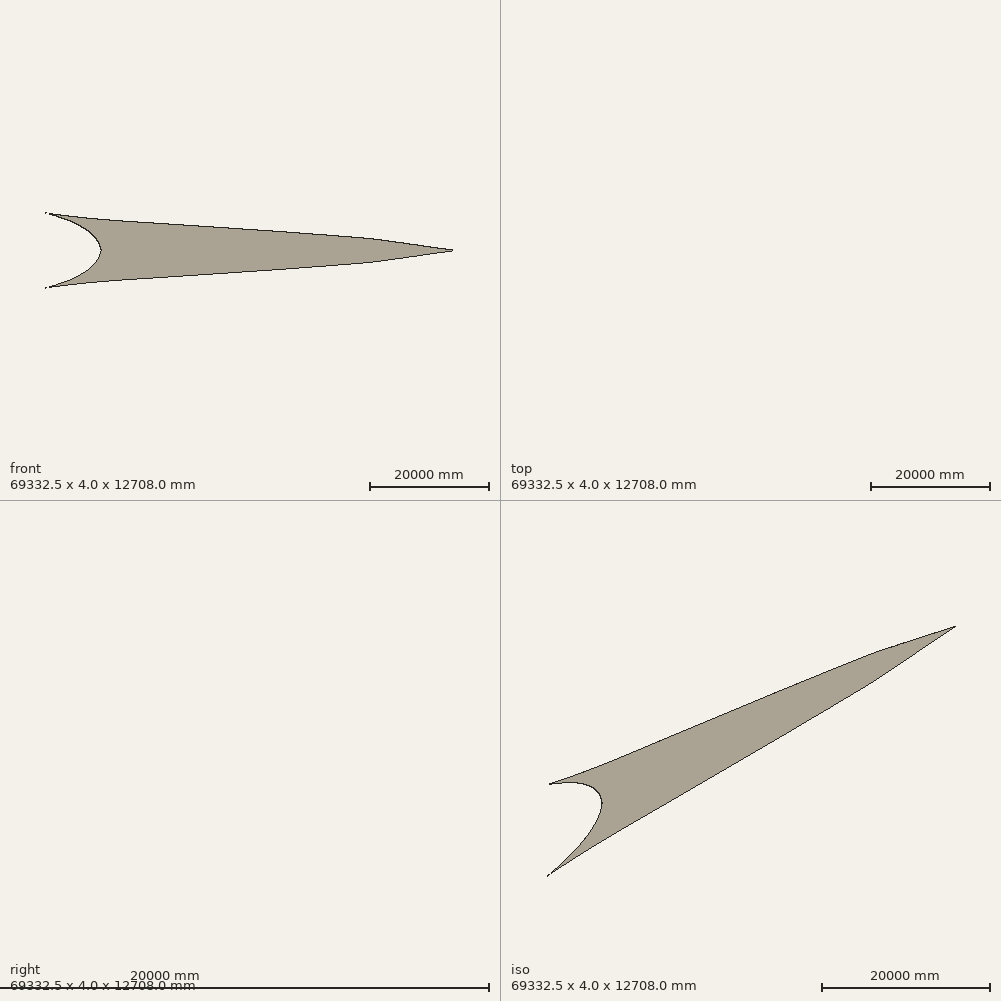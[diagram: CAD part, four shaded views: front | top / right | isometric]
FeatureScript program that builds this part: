
annotation { "Feature Type Name" : "Feature", "Feature Type Description" : "" }
export const myFeature = defineFeature(function(context is Context, id is Id, definition is map)
    precondition{}
    {
        {
            var Q0;
            Q0=qCreatedBy(makeId("Front.planeOp"),FACE);
            var sketch = newSketch(context, id + "F0", { "sketchPlane" : qUnion([Q0])});
            skLineSegment(sketch, "E0", {"start": v(34666.25, 0) * mm, "end": v(34435.52, -40.51) * mm});
            skLineSegment(sketch, "E1", {"start": v(34435.52, -40.51) * mm, "end": v(33954, -111.84) * mm});
            skLineSegment(sketch, "E2", {"start": v(33954, -111.84) * mm, "end": v(33694.2, -143.51) * mm});
            skLineSegment(sketch, "E3", {"start": v(33694.2, -143.51) * mm, "end": v(33434.53, -176) * mm});
            skLineSegment(sketch, "E4", {"start": v(33434.53, -176) * mm, "end": v(33084.57, -227.86) * mm});
            skLineSegment(sketch, "E5", {"start": v(33084.57, -227.86) * mm, "end": v(32734.78, -281.15) * mm});
            skLineSegment(sketch, "E6", {"start": v(32734.78, -281.15) * mm, "end": v(32207.2, -349.73) * mm});
            skLineSegment(sketch, "E7", {"start": v(32207.2, -349.73) * mm, "end": v(31403.65, -459.2) * mm});
            skLineSegment(sketch, "E8", {"start": v(31403.65, -459.2) * mm, "end": v(31005.5, -519.4) * mm});
            skLineSegment(sketch, "E9", {"start": v(31005.5, -519.4) * mm, "end": v(30607.23, -578.56) * mm});
            skLineSegment(sketch, "E10", {"start": v(30607.23, -578.56) * mm, "end": v(30171.5, -637.67) * mm});
            skLineSegment(sketch, "E11", {"start": v(30171.5, -637.67) * mm, "end": v(29735.68, -696.42) * mm});
            skLineSegment(sketch, "E12", {"start": v(29735.68, -696.42) * mm, "end": v(29204.16, -775.3) * mm});
            skLineSegment(sketch, "E13", {"start": v(29204.16, -775.3) * mm, "end": v(28673, -856.67) * mm});
            skLineSegment(sketch, "E14", {"start": v(28673, -856.67) * mm, "end": v(27858.21, -972.72) * mm});
            skLineSegment(sketch, "E15", {"start": v(27858.21, -972.72) * mm, "end": v(27293.5, -1049.15) * mm});
            skLineSegment(sketch, "E16", {"start": v(27293.5, -1049.15) * mm, "end": v(26729.36, -1129.59) * mm});
            skLineSegment(sketch, "E17", {"start": v(26729.36, -1129.59) * mm, "end": v(26203.07, -1212.27) * mm});
            skLineSegment(sketch, "E18", {"start": v(26203.07, -1212.27) * mm, "end": v(25676.63, -1293.72) * mm});
            skLineSegment(sketch, "E19", {"start": v(25676.63, -1293.72) * mm, "end": v(25053.6, -1378.03) * mm});
            skLineSegment(sketch, "E20", {"start": v(25053.6, -1378.03) * mm, "end": v(24429.9, -1457.76) * mm});
            skLineSegment(sketch, "E21", {"start": v(24429.9, -1457.76) * mm, "end": v(23395.89, -1601.9) * mm});
            skLineSegment(sketch, "E22", {"start": v(23395.89, -1601.9) * mm, "end": v(22319.9, -1757.22) * mm});
            skLineSegment(sketch, "E23", {"start": v(22319.9, -1757.22) * mm, "end": v(21652.28, -1849.27) * mm});
            skLineSegment(sketch, "E24", {"start": v(21652.28, -1849.27) * mm, "end": v(21071.92, -1921.36) * mm});
            skLineSegment(sketch, "E25", {"start": v(21071.92, -1921.36) * mm, "end": v(21056.24, -1795.32) * mm});
            skLineSegment(sketch, "E26", {"start": v(21056.24, -1795.32) * mm, "end": v(21071.92, -1921.36) * mm});
            skLineSegment(sketch, "E27", {"start": v(21071.92, -1921.36) * mm, "end": v(20056.25, -2031.26) * mm});
            skLineSegment(sketch, "E28", {"start": v(20056.25, -2031.26) * mm, "end": v(19038.87, -2123.26) * mm});
            skLineSegment(sketch, "E29", {"start": v(19038.87, -2123.26) * mm, "end": v(18478.8, -2165.3) * mm});
            skLineSegment(sketch, "E30", {"start": v(18478.8, -2165.3) * mm, "end": v(17918.73, -2207.13) * mm});
            skLineSegment(sketch, "E31", {"start": v(17918.73, -2207.13) * mm, "end": v(17198.26, -2267.71) * mm});
            skLineSegment(sketch, "E32", {"start": v(17198.26, -2267.71) * mm, "end": v(16477.82, -2328.44) * mm});
            skLineSegment(sketch, "E33", {"start": v(16477.82, -2328.44) * mm, "end": v(15811.55, -2378.05) * mm});
            skLineSegment(sketch, "E34", {"start": v(15811.55, -2378.05) * mm, "end": v(15145.33, -2427.68) * mm});
            skLineSegment(sketch, "E35", {"start": v(15145.33, -2427.68) * mm, "end": v(14404.67, -2491.2) * mm});
            skLineSegment(sketch, "E36", {"start": v(14404.67, -2491.2) * mm, "end": v(13664.34, -2559.4) * mm});
            skLineSegment(sketch, "E37", {"start": v(13664.34, -2559.4) * mm, "end": v(13197.36, -2600.88) * mm});
            skLineSegment(sketch, "E38", {"start": v(13197.36, -2600.88) * mm, "end": v(12729.92, -2635.53) * mm});
            skLineSegment(sketch, "E39", {"start": v(12729.92, -2635.53) * mm, "end": v(12355.32, -2656.4) * mm});
            skLineSegment(sketch, "E40", {"start": v(12355.32, -2656.4) * mm, "end": v(11980.8, -2678.66) * mm});
            skLineSegment(sketch, "E41", {"start": v(11980.8, -2678.66) * mm, "end": v(11669.47, -2702.74) * mm});
            skLineSegment(sketch, "E42", {"start": v(11669.47, -2702.74) * mm, "end": v(11358.04, -2725.72) * mm});
            skLineSegment(sketch, "E43", {"start": v(11358.04, -2725.72) * mm, "end": v(11136.43, -2737.82) * mm});
            skLineSegment(sketch, "E44", {"start": v(11136.43, -2737.82) * mm, "end": v(11129.52, -2611.02) * mm});
            skLineSegment(sketch, "E45", {"start": v(11129.52, -2611.02) * mm, "end": v(11136.43, -2737.82) * mm});
            skLineSegment(sketch, "E46", {"start": v(11136.43, -2737.82) * mm, "end": v(9910.14, -2828.29) * mm});
            skLineSegment(sketch, "E47", {"start": v(9910.14, -2828.29) * mm, "end": v(8060.9, -2971.75) * mm});
            skLineSegment(sketch, "E48", {"start": v(8060.9, -2971.75) * mm, "end": v(6295.9, -3108.8) * mm});
            skLineSegment(sketch, "E49", {"start": v(6295.9, -3108.8) * mm, "end": v(4314.32, -3255.54) * mm});
            skLineSegment(sketch, "E50", {"start": v(4314.32, -3255.54) * mm, "end": v(3195.55, -3329.79) * mm});
            skLineSegment(sketch, "E51", {"start": v(3195.55, -3329.79) * mm, "end": v(2076.63, -3401.7) * mm});
            skLineSegment(sketch, "E52", {"start": v(2076.63, -3401.7) * mm, "end": v(-54.58, -3545.08) * mm});
            skLineSegment(sketch, "E53", {"start": v(-54.58, -3545.08) * mm, "end": v(-2843.89, -3738.07) * mm});
            skLineSegment(sketch, "E54", {"start": v(-2843.89, -3738.07) * mm, "end": v(-5496.08, -3921.66) * mm});
            skLineSegment(sketch, "E55", {"start": v(-5496.08, -3921.66) * mm, "end": v(-8635.52, -4128.92) * mm});
            skLineSegment(sketch, "E56", {"start": v(-8635.52, -4128.92) * mm, "end": v(-10557.64, -4256.68) * mm});
            skLineSegment(sketch, "E57", {"start": v(-10557.64, -4256.68) * mm, "end": v(-12388.44, -4385.97) * mm});
            skLineSegment(sketch, "E58", {"start": v(-12388.44, -4385.97) * mm, "end": v(-12397.38, -4259.3) * mm});
            skLineSegment(sketch, "E59", {"start": v(-12397.38, -4259.3) * mm, "end": v(-12388.44, -4385.97) * mm});
            skLineSegment(sketch, "E60", {"start": v(-12388.44, -4385.97) * mm, "end": v(-14818.08, -4547.8) * mm});
            skLineSegment(sketch, "E61", {"start": v(-14818.08, -4547.8) * mm, "end": v(-18494.4, -4780.64) * mm});
            skLineSegment(sketch, "E62", {"start": v(-18494.4, -4780.64) * mm, "end": v(-20839.56, -4934.23) * mm});
            skLineSegment(sketch, "E63", {"start": v(-20839.56, -4934.23) * mm, "end": v(-23183.77, -5101.51) * mm});
            skLineSegment(sketch, "E64", {"start": v(-23183.77, -5101.51) * mm, "end": v(-24820.07, -5230.52) * mm});
            skLineSegment(sketch, "E65", {"start": v(-24820.07, -5230.52) * mm, "end": v(-26455.2, -5373.01) * mm});
            skLineSegment(sketch, "E66", {"start": v(-26455.2, -5373.01) * mm, "end": v(-27418.2, -5464.5) * mm});
            skLineSegment(sketch, "E67", {"start": v(-27418.2, -5464.5) * mm, "end": v(-28380.66, -5561.86) * mm});
            skLineSegment(sketch, "E68", {"start": v(-28380.66, -5561.86) * mm, "end": v(-29873.6, -5724.83) * mm});
            skLineSegment(sketch, "E69", {"start": v(-29873.6, -5724.83) * mm, "end": v(-31364.83, -5902.73) * mm});
            skLineSegment(sketch, "E70", {"start": v(-31364.83, -5902.73) * mm, "end": v(-32425.77, -6038.88) * mm});
            skLineSegment(sketch, "E71", {"start": v(-32425.77, -6038.88) * mm, "end": v(-33485.6, -6183.17) * mm});
            skLineSegment(sketch, "E72", {"start": v(-33485.6, -6183.17) * mm, "end": v(-34666.25, -6354.01) * mm});
            skLineSegment(sketch, "E73", {"start": v(-34666.25, -6354.01) * mm, "end": v(-34222.2, -6227.2) * mm});
            skLineSegment(sketch, "E74", {"start": v(-34222.2, -6227.2) * mm, "end": v(-33534.96, -6035.45) * mm});
            skLineSegment(sketch, "E75", {"start": v(-33534.96, -6035.45) * mm, "end": v(-33260.49, -5958) * mm});
            skLineSegment(sketch, "E76", {"start": v(-33260.49, -5958) * mm, "end": v(-32987.87, -5874.54) * mm});
            skLineSegment(sketch, "E77", {"start": v(-32987.87, -5874.54) * mm, "end": v(-32730.85, -5786.25) * mm});
            skLineSegment(sketch, "E78", {"start": v(-32730.85, -5786.25) * mm, "end": v(-32474.71, -5695.21) * mm});
            skLineSegment(sketch, "E79", {"start": v(-32474.71, -5695.21) * mm, "end": v(-32205.42, -5603.21) * mm});
            skLineSegment(sketch, "E80", {"start": v(-32205.42, -5603.21) * mm, "end": v(-31936, -5511.75) * mm});
            skLineSegment(sketch, "E81", {"start": v(-31936, -5511.75) * mm, "end": v(-31454.3, -5342.26) * mm});
            skLineSegment(sketch, "E82", {"start": v(-31454.3, -5342.26) * mm, "end": v(-31090.18, -5216.8) * mm});
            skLineSegment(sketch, "E83", {"start": v(-31090.18, -5216.8) * mm, "end": v(-30730.42, -5080.79) * mm});
            skLineSegment(sketch, "E84", {"start": v(-30730.42, -5080.79) * mm, "end": v(-30450.56, -4956.63) * mm});
            skLineSegment(sketch, "E85", {"start": v(-30450.56, -4956.63) * mm, "end": v(-30172.5, -4827.83) * mm});
            skLineSegment(sketch, "E86", {"start": v(-30172.5, -4827.83) * mm, "end": v(-29864.13, -4691.68) * mm});
            skLineSegment(sketch, "E87", {"start": v(-29864.13, -4691.68) * mm, "end": v(-29557.07, -4553.08) * mm});
            skLineSegment(sketch, "E88", {"start": v(-29557.07, -4553.08) * mm, "end": v(-29195.2, -4369.4) * mm});
            skLineSegment(sketch, "E89", {"start": v(-29195.2, -4369.4) * mm, "end": v(-28840.25, -4172.03) * mm});
            skLineSegment(sketch, "E90", {"start": v(-28840.25, -4172.03) * mm, "end": v(-28508.9, -3979.75) * mm});
            skLineSegment(sketch, "E91", {"start": v(-28508.9, -3979.75) * mm, "end": v(-28181.1, -3781.7) * mm});
            skLineSegment(sketch, "E92", {"start": v(-28181.1, -3781.7) * mm, "end": v(-27807.87, -3542.59) * mm});
            skLineSegment(sketch, "E93", {"start": v(-27807.87, -3542.59) * mm, "end": v(-27445.64, -3287.24) * mm});
            skLineSegment(sketch, "E94", {"start": v(-27445.64, -3287.24) * mm, "end": v(-27192.9, -3088.72) * mm});
            skLineSegment(sketch, "E95", {"start": v(-27192.9, -3088.72) * mm, "end": v(-26950.31, -2878.1) * mm});
            skLineSegment(sketch, "E96", {"start": v(-26950.31, -2878.1) * mm, "end": v(-26773.48, -2710.51) * mm});
            skLineSegment(sketch, "E97", {"start": v(-26773.48, -2710.51) * mm, "end": v(-26600.89, -2538.4) * mm});
            skLineSegment(sketch, "E98", {"start": v(-26600.89, -2538.4) * mm, "end": v(-26443.36, -2376.02) * mm});
            skLineSegment(sketch, "E99", {"start": v(-26443.36, -2376.02) * mm, "end": v(-26291.34, -2208.6) * mm});
            skLineSegment(sketch, "E100", {"start": v(-26291.34, -2208.6) * mm, "end": v(-26141.4, -2025.37) * mm});
            skLineSegment(sketch, "E101", {"start": v(-26141.4, -2025.37) * mm, "end": v(-26000.4, -1835.18) * mm});
            skLineSegment(sketch, "E102", {"start": v(-26000.4, -1835.18) * mm, "end": v(-25853.82, -1619.05) * mm});
            skLineSegment(sketch, "E103", {"start": v(-25853.82, -1619.05) * mm, "end": v(-25717.1, -1395.86) * mm});
            skLineSegment(sketch, "E104", {"start": v(-25717.1, -1395.86) * mm, "end": v(-25606.9, -1189.89) * mm});
            skLineSegment(sketch, "E105", {"start": v(-25606.9, -1189.89) * mm, "end": v(-25521.49, -973.79) * mm});
            skLineSegment(sketch, "E106", {"start": v(-25521.49, -973.79) * mm, "end": v(-25498.04, -890.2) * mm});
            skLineSegment(sketch, "E107", {"start": v(-25498.04, -890.2) * mm, "end": v(-25473.84, -806.8) * mm});
            skLineSegment(sketch, "E108", {"start": v(-25473.84, -806.8) * mm, "end": v(-25430.5, -689.76) * mm});
            skLineSegment(sketch, "E109", {"start": v(-25430.5, -689.76) * mm, "end": v(-25388.04, -572.57) * mm});
            skLineSegment(sketch, "E110", {"start": v(-25388.04, -572.57) * mm, "end": v(-25362.3, -474.62) * mm});
            skLineSegment(sketch, "E111", {"start": v(-25362.3, -474.62) * mm, "end": v(-25339.1, -375.77) * mm});
            skLineSegment(sketch, "E112", {"start": v(-25339.1, -375.77) * mm, "end": v(-25315.47, -287.12) * mm});
            skLineSegment(sketch, "E113", {"start": v(-25315.47, -287.12) * mm, "end": v(-25294.31, -198.04) * mm});
            skLineSegment(sketch, "E114", {"start": v(-25294.31, -198.04) * mm, "end": v(-25280.7, -99.52) * mm});
            skLineSegment(sketch, "E115", {"start": v(-25280.7, -99.52) * mm, "end": v(-25275.84, 0) * mm});
            skLineSegment(sketch, "E116", {"start": v(-25275.84, 0) * mm, "end": v(-25149, -6.17) * mm});
            skLineSegment(sketch, "E117", {"start": v(-25149, -6.17) * mm, "end": v(-25275.84, 0) * mm});
            skLineSegment(sketch, "E118", {"start": v(-25275.84, 0) * mm, "end": v(-25280.7, 99.5) * mm});
            skLineSegment(sketch, "E119", {"start": v(-25280.7, 99.5) * mm, "end": v(-25294.31, 198.04) * mm});
            skLineSegment(sketch, "E120", {"start": v(-25294.31, 198.04) * mm, "end": v(-25315.47, 287.12) * mm});
            skLineSegment(sketch, "E121", {"start": v(-25315.47, 287.12) * mm, "end": v(-25339.1, 375.77) * mm});
            skLineSegment(sketch, "E122", {"start": v(-25339.1, 375.77) * mm, "end": v(-25362.3, 474.62) * mm});
            skLineSegment(sketch, "E123", {"start": v(-25362.3, 474.62) * mm, "end": v(-25388.04, 572.57) * mm});
            skLineSegment(sketch, "E124", {"start": v(-25388.04, 572.57) * mm, "end": v(-25430.5, 689.76) * mm});
            skLineSegment(sketch, "E125", {"start": v(-25430.5, 689.76) * mm, "end": v(-25473.84, 806.8) * mm});
            skLineSegment(sketch, "E126", {"start": v(-25473.84, 806.8) * mm, "end": v(-25498.04, 890.2) * mm});
            skLineSegment(sketch, "E127", {"start": v(-25498.04, 890.2) * mm, "end": v(-25521.49, 973.79) * mm});
            skLineSegment(sketch, "E128", {"start": v(-25521.49, 973.79) * mm, "end": v(-25606.9, 1189.89) * mm});
            skLineSegment(sketch, "E129", {"start": v(-25606.9, 1189.89) * mm, "end": v(-25717.1, 1395.86) * mm});
            skLineSegment(sketch, "E130", {"start": v(-25717.1, 1395.86) * mm, "end": v(-25853.82, 1619.02) * mm});
            skLineSegment(sketch, "E131", {"start": v(-25853.82, 1619.02) * mm, "end": v(-26000.4, 1835.18) * mm});
            skLineSegment(sketch, "E132", {"start": v(-26000.4, 1835.18) * mm, "end": v(-26141.4, 2025.37) * mm});
            skLineSegment(sketch, "E133", {"start": v(-26141.4, 2025.37) * mm, "end": v(-26291.34, 2208.6) * mm});
            skLineSegment(sketch, "E134", {"start": v(-26291.34, 2208.6) * mm, "end": v(-26443.36, 2376) * mm});
            skLineSegment(sketch, "E135", {"start": v(-26443.36, 2376) * mm, "end": v(-26600.89, 2538.4) * mm});
            skLineSegment(sketch, "E136", {"start": v(-26600.89, 2538.4) * mm, "end": v(-26773.48, 2710.51) * mm});
            skLineSegment(sketch, "E137", {"start": v(-26773.48, 2710.51) * mm, "end": v(-26950.31, 2878.07) * mm});
            skLineSegment(sketch, "E138", {"start": v(-26950.31, 2878.07) * mm, "end": v(-27192.9, 3088.72) * mm});
            skLineSegment(sketch, "E139", {"start": v(-27192.9, 3088.72) * mm, "end": v(-27445.64, 3287.22) * mm});
            skLineSegment(sketch, "E140", {"start": v(-27445.64, 3287.22) * mm, "end": v(-27807.87, 3542.59) * mm});
            skLineSegment(sketch, "E141", {"start": v(-27807.87, 3542.59) * mm, "end": v(-28181.1, 3781.7) * mm});
            skLineSegment(sketch, "E142", {"start": v(-28181.1, 3781.7) * mm, "end": v(-28508.9, 3979.75) * mm});
            skLineSegment(sketch, "E143", {"start": v(-28508.9, 3979.75) * mm, "end": v(-28840.25, 4172.03) * mm});
            skLineSegment(sketch, "E144", {"start": v(-28840.25, 4172.03) * mm, "end": v(-29195.2, 4369.4) * mm});
            skLineSegment(sketch, "E145", {"start": v(-29195.2, 4369.4) * mm, "end": v(-29557.07, 4553.08) * mm});
            skLineSegment(sketch, "E146", {"start": v(-29557.07, 4553.08) * mm, "end": v(-29864.13, 4691.68) * mm});
            skLineSegment(sketch, "E147", {"start": v(-29864.13, 4691.68) * mm, "end": v(-30172.5, 4827.8) * mm});
            skLineSegment(sketch, "E148", {"start": v(-30172.5, 4827.8) * mm, "end": v(-30450.56, 4956.63) * mm});
            skLineSegment(sketch, "E149", {"start": v(-30450.56, 4956.63) * mm, "end": v(-30730.42, 5080.79) * mm});
            skLineSegment(sketch, "E150", {"start": v(-30730.42, 5080.79) * mm, "end": v(-31090.18, 5216.8) * mm});
            skLineSegment(sketch, "E151", {"start": v(-31090.18, 5216.8) * mm, "end": v(-31454.3, 5342.26) * mm});
            skLineSegment(sketch, "E152", {"start": v(-31454.3, 5342.26) * mm, "end": v(-31936, 5511.75) * mm});
            skLineSegment(sketch, "E153", {"start": v(-31936, 5511.75) * mm, "end": v(-32205.42, 5603.21) * mm});
            skLineSegment(sketch, "E154", {"start": v(-32205.42, 5603.21) * mm, "end": v(-32474.71, 5695.21) * mm});
            skLineSegment(sketch, "E155", {"start": v(-32474.71, 5695.21) * mm, "end": v(-32730.85, 5786.25) * mm});
            skLineSegment(sketch, "E156", {"start": v(-32730.85, 5786.25) * mm, "end": v(-32987.87, 5874.51) * mm});
            skLineSegment(sketch, "E157", {"start": v(-32987.87, 5874.51) * mm, "end": v(-33260.49, 5957.98) * mm});
            skLineSegment(sketch, "E158", {"start": v(-33260.49, 5957.98) * mm, "end": v(-33534.96, 6035.45) * mm});
            skLineSegment(sketch, "E159", {"start": v(-33534.96, 6035.45) * mm, "end": v(-34222.2, 6227.17) * mm});
            skLineSegment(sketch, "E160", {"start": v(-34222.2, 6227.17) * mm, "end": v(-34666.25, 6354.01) * mm});
            skLineSegment(sketch, "E161", {"start": v(-34666.25, 6354.01) * mm, "end": v(-33485.6, 6183.17) * mm});
            skLineSegment(sketch, "E162", {"start": v(-33485.6, 6183.17) * mm, "end": v(-32425.77, 6038.88) * mm});
            skLineSegment(sketch, "E163", {"start": v(-32425.77, 6038.88) * mm, "end": v(-31364.83, 5902.73) * mm});
            skLineSegment(sketch, "E164", {"start": v(-31364.83, 5902.73) * mm, "end": v(-29873.6, 5724.83) * mm});
            skLineSegment(sketch, "E165", {"start": v(-29873.6, 5724.83) * mm, "end": v(-28380.66, 5561.84) * mm});
            skLineSegment(sketch, "E166", {"start": v(-28380.66, 5561.84) * mm, "end": v(-27418.2, 5464.5) * mm});
            skLineSegment(sketch, "E167", {"start": v(-27418.2, 5464.5) * mm, "end": v(-26455.2, 5373.01) * mm});
            skLineSegment(sketch, "E168", {"start": v(-26455.2, 5373.01) * mm, "end": v(-24820.07, 5230.52) * mm});
            skLineSegment(sketch, "E169", {"start": v(-24820.07, 5230.52) * mm, "end": v(-23183.77, 5101.51) * mm});
            skLineSegment(sketch, "E170", {"start": v(-23183.77, 5101.51) * mm, "end": v(-20839.56, 4934.23) * mm});
            skLineSegment(sketch, "E171", {"start": v(-20839.56, 4934.23) * mm, "end": v(-18494.4, 4780.64) * mm});
            skLineSegment(sketch, "E172", {"start": v(-18494.4, 4780.64) * mm, "end": v(-14818.08, 4547.8) * mm});
            skLineSegment(sketch, "E173", {"start": v(-14818.08, 4547.8) * mm, "end": v(-12388.44, 4385.97) * mm});
            skLineSegment(sketch, "E174", {"start": v(-12388.44, 4385.97) * mm, "end": v(-12396.9, 4259.25) * mm});
            skLineSegment(sketch, "E175", {"start": v(-12396.9, 4259.25) * mm, "end": v(-12388.44, 4385.97) * mm});
            skLineSegment(sketch, "E176", {"start": v(-12388.44, 4385.97) * mm, "end": v(-10557.64, 4256.68) * mm});
            skLineSegment(sketch, "E177", {"start": v(-10557.64, 4256.68) * mm, "end": v(-8635.52, 4128.92) * mm});
            skLineSegment(sketch, "E178", {"start": v(-8635.52, 4128.92) * mm, "end": v(-5496.08, 3921.66) * mm});
            skLineSegment(sketch, "E179", {"start": v(-5496.08, 3921.66) * mm, "end": v(-2843.89, 3738.04) * mm});
            skLineSegment(sketch, "E180", {"start": v(-2843.89, 3738.04) * mm, "end": v(-54.58, 3545.08) * mm});
            skLineSegment(sketch, "E181", {"start": v(-54.58, 3545.08) * mm, "end": v(2076.63, 3401.67) * mm});
            skLineSegment(sketch, "E182", {"start": v(2076.63, 3401.67) * mm, "end": v(3195.55, 3329.79) * mm});
            skLineSegment(sketch, "E183", {"start": v(3195.55, 3329.79) * mm, "end": v(4314.32, 3255.54) * mm});
            skLineSegment(sketch, "E184", {"start": v(4314.32, 3255.54) * mm, "end": v(6295.9, 3108.8) * mm});
            skLineSegment(sketch, "E185", {"start": v(6295.9, 3108.8) * mm, "end": v(8060.9, 2971.75) * mm});
            skLineSegment(sketch, "E186", {"start": v(8060.9, 2971.75) * mm, "end": v(9910.14, 2828.3) * mm});
            skLineSegment(sketch, "E187", {"start": v(9910.14, 2828.3) * mm, "end": v(11136.43, 2737.82) * mm});
            skLineSegment(sketch, "E188", {"start": v(11136.43, 2737.82) * mm, "end": v(11127.08, 2611.17) * mm});
            skLineSegment(sketch, "E189", {"start": v(11127.08, 2611.17) * mm, "end": v(11136.43, 2737.82) * mm});
            skLineSegment(sketch, "E190", {"start": v(11136.43, 2737.82) * mm, "end": v(11358.04, 2725.72) * mm});
            skLineSegment(sketch, "E191", {"start": v(11358.04, 2725.72) * mm, "end": v(11669.47, 2702.74) * mm});
            skLineSegment(sketch, "E192", {"start": v(11669.47, 2702.74) * mm, "end": v(11980.8, 2678.66) * mm});
            skLineSegment(sketch, "E193", {"start": v(11980.8, 2678.66) * mm, "end": v(12355.32, 2656.4) * mm});
            skLineSegment(sketch, "E194", {"start": v(12355.32, 2656.4) * mm, "end": v(12729.9, 2635.5) * mm});
            skLineSegment(sketch, "E195", {"start": v(12729.9, 2635.5) * mm, "end": v(13197.36, 2600.88) * mm});
            skLineSegment(sketch, "E196", {"start": v(13197.36, 2600.88) * mm, "end": v(13664.34, 2559.4) * mm});
            skLineSegment(sketch, "E197", {"start": v(13664.34, 2559.4) * mm, "end": v(14404.67, 2491.2) * mm});
            skLineSegment(sketch, "E198", {"start": v(14404.67, 2491.2) * mm, "end": v(15145.33, 2427.68) * mm});
            skLineSegment(sketch, "E199", {"start": v(15145.33, 2427.68) * mm, "end": v(15811.55, 2378.02) * mm});
            skLineSegment(sketch, "E200", {"start": v(15811.55, 2378.02) * mm, "end": v(16477.82, 2328.44) * mm});
            skLineSegment(sketch, "E201", {"start": v(16477.82, 2328.44) * mm, "end": v(17198.26, 2267.71) * mm});
            skLineSegment(sketch, "E202", {"start": v(17198.26, 2267.71) * mm, "end": v(17918.73, 2207.13) * mm});
            skLineSegment(sketch, "E203", {"start": v(17918.73, 2207.13) * mm, "end": v(18478.8, 2165.3) * mm});
            skLineSegment(sketch, "E204", {"start": v(18478.8, 2165.3) * mm, "end": v(19038.87, 2123.24) * mm});
            skLineSegment(sketch, "E205", {"start": v(19038.87, 2123.24) * mm, "end": v(20056.25, 2031.26) * mm});
            skLineSegment(sketch, "E206", {"start": v(20056.25, 2031.26) * mm, "end": v(21071.92, 1921.36) * mm});
            skLineSegment(sketch, "E207", {"start": v(21071.92, 1921.36) * mm, "end": v(21058.25, 1795.1) * mm});
            skLineSegment(sketch, "E208", {"start": v(21058.25, 1795.1) * mm, "end": v(21071.92, 1921.36) * mm});
            skLineSegment(sketch, "E209", {"start": v(21071.92, 1921.36) * mm, "end": v(21652.28, 1849.27) * mm});
            skLineSegment(sketch, "E210", {"start": v(21652.28, 1849.27) * mm, "end": v(22319.9, 1757.22) * mm});
            skLineSegment(sketch, "E211", {"start": v(22319.9, 1757.22) * mm, "end": v(23395.89, 1601.9) * mm});
            skLineSegment(sketch, "E212", {"start": v(23395.89, 1601.9) * mm, "end": v(24429.9, 1457.76) * mm});
            skLineSegment(sketch, "E213", {"start": v(24429.9, 1457.76) * mm, "end": v(25053.6, 1378.03) * mm});
            skLineSegment(sketch, "E214", {"start": v(25053.6, 1378.03) * mm, "end": v(25676.63, 1293.72) * mm});
            skLineSegment(sketch, "E215", {"start": v(25676.63, 1293.72) * mm, "end": v(26203.07, 1212.27) * mm});
            skLineSegment(sketch, "E216", {"start": v(26203.07, 1212.27) * mm, "end": v(26729.36, 1129.59) * mm});
            skLineSegment(sketch, "E217", {"start": v(26729.36, 1129.59) * mm, "end": v(27293.5, 1049.12) * mm});
            skLineSegment(sketch, "E218", {"start": v(27293.5, 1049.12) * mm, "end": v(27858.21, 972.72) * mm});
            skLineSegment(sketch, "E219", {"start": v(27858.21, 972.72) * mm, "end": v(28673, 856.67) * mm});
            skLineSegment(sketch, "E220", {"start": v(28673, 856.67) * mm, "end": v(29204.16, 775.28) * mm});
            skLineSegment(sketch, "E221", {"start": v(29204.16, 775.28) * mm, "end": v(29735.68, 696.42) * mm});
            skLineSegment(sketch, "E222", {"start": v(29735.68, 696.42) * mm, "end": v(30171.5, 637.67) * mm});
            skLineSegment(sketch, "E223", {"start": v(30171.5, 637.67) * mm, "end": v(30607.23, 578.56) * mm});
            skLineSegment(sketch, "E224", {"start": v(30607.23, 578.56) * mm, "end": v(31005.5, 519.4) * mm});
            skLineSegment(sketch, "E225", {"start": v(31005.5, 519.4) * mm, "end": v(31403.65, 459.2) * mm});
            skLineSegment(sketch, "E226", {"start": v(31403.65, 459.2) * mm, "end": v(32207.2, 349.73) * mm});
            skLineSegment(sketch, "E227", {"start": v(32207.2, 349.73) * mm, "end": v(32734.78, 281.15) * mm});
            skLineSegment(sketch, "E228", {"start": v(32734.78, 281.15) * mm, "end": v(33084.57, 227.86) * mm});
            skLineSegment(sketch, "E229", {"start": v(33084.57, 227.86) * mm, "end": v(33434.53, 175.97) * mm});
            skLineSegment(sketch, "E230", {"start": v(33434.53, 175.97) * mm, "end": v(33694.2, 143.51) * mm});
            skLineSegment(sketch, "E231", {"start": v(33694.2, 143.51) * mm, "end": v(33954, 111.84) * mm});
            skLineSegment(sketch, "E232", {"start": v(33954, 111.84) * mm, "end": v(34435.52, 40.49) * mm});
            skLineSegment(sketch, "E233", {"start": v(34435.52, 40.49) * mm, "end": v(34666.25, 0) * mm});
            skSolve(sketch);
        }
        {
            var Q0;
            Q0 = qSketchRegion(id + "F0", true);
            extrude(context, id + "F1", {"entities" : qUnion([Q0]), "depth" : 4 * mm, "offsetDistance" : 25 * mm});
        }
    });
